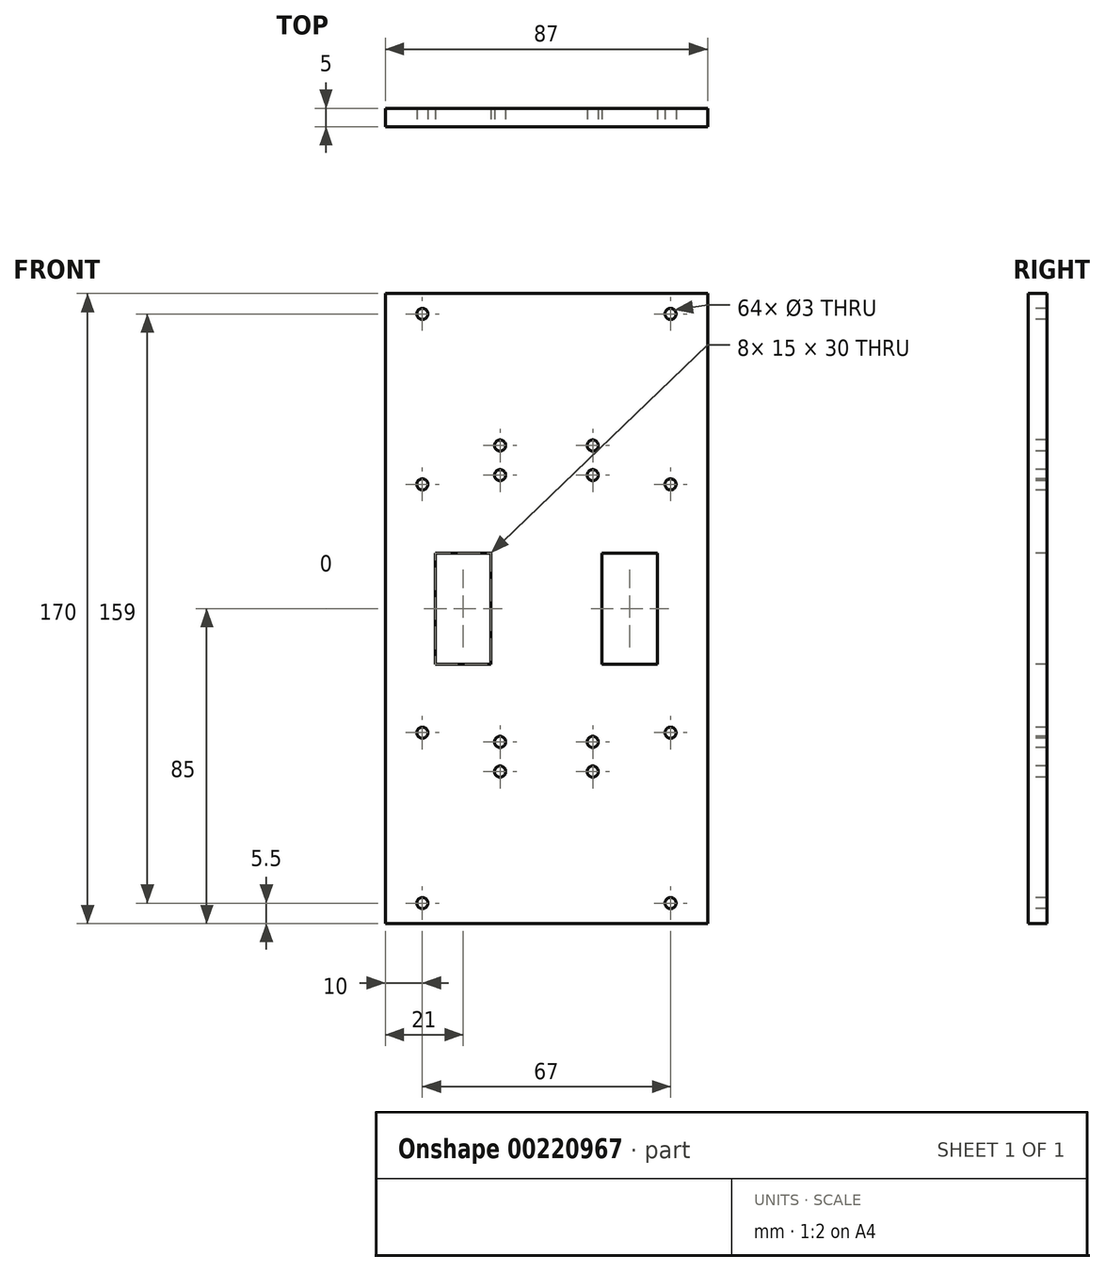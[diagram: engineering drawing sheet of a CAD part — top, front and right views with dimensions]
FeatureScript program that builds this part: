
annotation { "Feature Type Name" : "Feature", "Feature Type Description" : "" }
export const myFeature = defineFeature(function(context is Context, id is Id, definition is map)
    precondition{}
    {
        {
            var Q0;
            Q0=qCreatedBy(makeId("Front.planeOp"),FACE);
            var sketch = newSketch(context, id + "F0", { "sketchPlane" : qUnion([Q0])});
            skLineSegment(sketch, "E0.bottom", {"start": v(0, 0) * mm, "end": v(87, 0) * mm});
            skLineSegment(sketch, "E0.top", {"start": v(0, 170) * mm, "end": v(87, 170) * mm});
            skLineSegment(sketch, "E0.left", {"start": v(0, 0) * mm, "end": v(0, 170) * mm});
            skLineSegment(sketch, "E0.right", {"start": v(87, 0) * mm, "end": v(87, 170) * mm});
            skSolve(sketch);
        }
        {
            var Q0;
            Q0=makeQuery(id+"F0.imprint","IMPRINT",FACE,{"disambiguationData":[TD([[makeQuery(id+"F0.imprint","IMPRINT",EDGE,{"derivedFrom":sQuery(id+"F0.wireOp",EDGE,"E0.bottom")}),1.0]])]});
            extrude(context, id + "F1", {"entities" : qUnion([Q0]), "depth" : 5 * mm, "offsetDistance" : 25 * mm});
        }
        {
            var Q0;
            Q0=makeQuery(id+"F1.opExtrude","CAP_FACE",FACE,{"disambiguationData":[OSD([sQuery(id+"F0.wireOp",EDGE,"E0.bottom"),sQuery(id+"F0.wireOp",EDGE,"E0.top"),sQuery(id+"F0.wireOp",EDGE,"E0.left"),sQuery(id+"F0.wireOp",EDGE,"E0.right")])],"isStart":false});
            var sketch = newSketch(context, id + "F2", { "sketchPlane" : qUnion([Q0])});
            skLineSegment(sketch, "E1", {"start": v(0, 0) * mm, "end": v(0, 5.5) * mm});
            skLineSegment(sketch, "E2", {"start": v(0, 5.5) * mm, "end": v(10, 5.5) * mm});
            skCircle(sketch, "E3", {"center": v(10, 5.5) * mm, "radius": 1.5 * mm});
            skLineSegment(sketch, "E4", {"start": v(87, 0) * mm, "end": v(87, 5.5) * mm});
            skLineSegment(sketch, "E5", {"start": v(87, 5.5) * mm, "end": v(77, 5.5) * mm});
            skCircle(sketch, "E6", {"center": v(77, 5.5) * mm, "radius": 1.5 * mm});
            skLineSegment(sketch, "E7", {"start": v(10, 5.5) * mm, "end": v(10, 51.5) * mm});
            skLineSegment(sketch, "E8", {"start": v(77, 5.5) * mm, "end": v(77, 51.5) * mm});
            skCircle(sketch, "E9", {"center": v(10, 51.5) * mm, "radius": 1.5 * mm});
            skCircle(sketch, "E10", {"center": v(77, 51.5) * mm, "radius": 1.5 * mm});
            skLineSegment(sketch, "E11", {"start": v(0, 170) * mm, "end": v(0, 164.5) * mm});
            skLineSegment(sketch, "E12", {"start": v(0, 164.5) * mm, "end": v(10, 164.5) * mm});
            skLineSegment(sketch, "E13", {"start": v(87, 170) * mm, "end": v(87, 164.5) * mm});
            skLineSegment(sketch, "E14", {"start": v(87, 164.5) * mm, "end": v(77, 164.5) * mm});
            skLineSegment(sketch, "E15", {"start": v(77, 164.5) * mm, "end": v(77, 118.5) * mm});
            skLineSegment(sketch, "E16", {"start": v(10, 164.5) * mm, "end": v(10, 118.5) * mm});
            skCircle(sketch, "E17", {"center": v(10, 164.5) * mm, "radius": 1.5 * mm});
            skCircle(sketch, "E18", {"center": v(77, 164.5) * mm, "radius": 1.5 * mm});
            skCircle(sketch, "E19", {"center": v(77, 118.5) * mm, "radius": 1.5 * mm});
            skCircle(sketch, "E20", {"center": v(10, 118.5) * mm, "radius": 1.5 * mm});
            skLineSegment(sketch, "E21", {"start": v(58.5, 70) * mm, "end": v(58.5, 100) * mm});
            skLineSegment(sketch, "E22", {"start": v(28.5, 100) * mm, "end": v(28.5, 70) * mm});
            skLineSegment(sketch, "E23", {"start": v(43.5, 100) * mm, "end": v(43.5, 125) * mm});
            skLineSegment(sketch, "E24", {"start": v(43.5, 125) * mm, "end": v(56, 125) * mm});
            skLineSegment(sketch, "E25", {"start": v(43.5, 125) * mm, "end": v(31, 125) * mm});
            skLineSegment(sketch, "E26", {"start": v(31, 125) * mm, "end": v(31, 129) * mm});
            skLineSegment(sketch, "E27", {"start": v(31, 125) * mm, "end": v(31, 121) * mm});
            skLineSegment(sketch, "E28", {"start": v(56, 125) * mm, "end": v(56, 129) * mm});
            skLineSegment(sketch, "E29", {"start": v(56, 125) * mm, "end": v(56, 121) * mm});
            skCircle(sketch, "E30", {"center": v(31, 129) * mm, "radius": 1.5 * mm});
            skCircle(sketch, "E31", {"center": v(31, 121) * mm, "radius": 1.5 * mm});
            skCircle(sketch, "E32", {"center": v(56, 121) * mm, "radius": 1.5 * mm});
            skCircle(sketch, "E33", {"center": v(56, 129) * mm, "radius": 1.5 * mm});
            skLineSegment(sketch, "E34", {"start": v(43.5, 70) * mm, "end": v(43.5, 45) * mm});
            skLineSegment(sketch, "E35", {"start": v(43.5, 45) * mm, "end": v(31, 45) * mm});
            skLineSegment(sketch, "E36", {"start": v(43.5, 45) * mm, "end": v(56, 45) * mm});
            skLineSegment(sketch, "E37", {"start": v(31, 45) * mm, "end": v(31, 49) * mm});
            skLineSegment(sketch, "E38", {"start": v(31, 45) * mm, "end": v(31, 41) * mm});
            skLineSegment(sketch, "E39", {"start": v(56, 45) * mm, "end": v(56, 41) * mm});
            skLineSegment(sketch, "E40", {"start": v(56, 45) * mm, "end": v(56, 49) * mm});
            skCircle(sketch, "E41", {"center": v(31, 49) * mm, "radius": 1.5 * mm});
            skCircle(sketch, "E42", {"center": v(31, 41) * mm, "radius": 1.5 * mm});
            skCircle(sketch, "E43", {"center": v(56, 41) * mm, "radius": 1.5 * mm});
            skCircle(sketch, "E44", {"center": v(56, 49) * mm, "radius": 1.5 * mm});
            skLineSegment(sketch, "E45", {"start": v(43.5, 100) * mm, "end": v(43.5, 70) * mm});
            skLineSegment(sketch, "E46", {"start": v(28.5, 100) * mm, "end": v(13.5, 100) * mm});
            skLineSegment(sketch, "E47", {"start": v(28.5, 70) * mm, "end": v(13.5, 70) * mm});
            skLineSegment(sketch, "E48", {"start": v(13.5, 70) * mm, "end": v(13.5, 100) * mm});
            skLineSegment(sketch, "E49", {"start": v(58.5, 100) * mm, "end": v(73.5, 100) * mm});
            skLineSegment(sketch, "E50", {"start": v(73.5, 100) * mm, "end": v(73.5, 70) * mm});
            skLineSegment(sketch, "E51", {"start": v(73.5, 70) * mm, "end": v(58.5, 70) * mm});
            skSolve(sketch);
        }
        {
            var Q0;
            Q0 = qSketchRegion(id + "F2", true);
            extrude(context, id + "F3", {"entities" : qUnion([Q0]), "operationType" : NewBodyOperationType.REMOVE, "oppositeDirection" : true, "depth" : 25 * mm, "offsetDistance" : 25 * mm});
        }
    });
